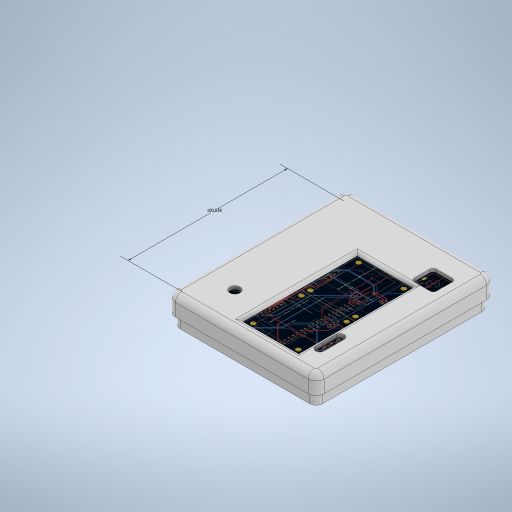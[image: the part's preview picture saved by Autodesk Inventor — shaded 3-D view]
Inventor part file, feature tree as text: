
AUTODESK INVENTOR PART (.ipt)
format: ipt  version: 2024.4 (Build 284460000, 460)  size: 840,192 bytes
history: native  units: mm
features: fillet x7, sketch x5, extrude x4, other x1
ambient origin geometry x8: Origin, YZ Plane, XZ Plane, XY Plane, X Axis, Y Axis, Z Axis, Center Point
bodies: Solid1 (feature_tree)
feature tree (17):
  sketch  "Sketch1"  dims[d3=100.838mm d4=50.419mm]
  extrude  "Extrusion1"  Depth=50.419mm
  extrude  "Extrusion2"  Depth=41.015212mm
  extrude  "Extrusion3"  Depth=2.0mm
  fillet  "Fillet3"  Radius=4.0mm
  fillet  "Fillet4"  Radius=4.0mm
  fillet  "Fillet5"  Radius=2.0mm
  extrude  "Extrusion4"  Depth=2.0mm TaperAngle=0.0deg
  fillet  "Fillet6"  Radius=2.0mm
  fillet  "Fillet7"  Radius=4.0mm
  fillet  "Fillet8"  Radius=2.6mm
  fillet  "Fillet9"  Radius=2.0mm
  other  "Image1"
  sketch  "Sketch2"  dims[d5=50.419mm d6=41.015212mm]
  sketch  "Sketch3"  dims[d7=41.015212mm d8=2.0mm d9=4.0mm d10=4.0mm d11=2.0mm]
  sketch  "Sketch4"  dims[d12=10.0mm d13=0.0mm d14=2.0mm d15=0.0mm d16=2.0mm d17=0.0mm d20=4.0mm d22=2.6mm d23=2.0mm]
  sketch  "Sketch6"  dims[d24=2.0mm d25=2.0mm d26=7.0mm d27=10.0mm d28=0.0mm d29=0.0mm d30=4.0mm d31=4.0mm d32=2.0mm d33=5.0mm d34=6.5mm d35=0.0mm d36=0.0mm]
